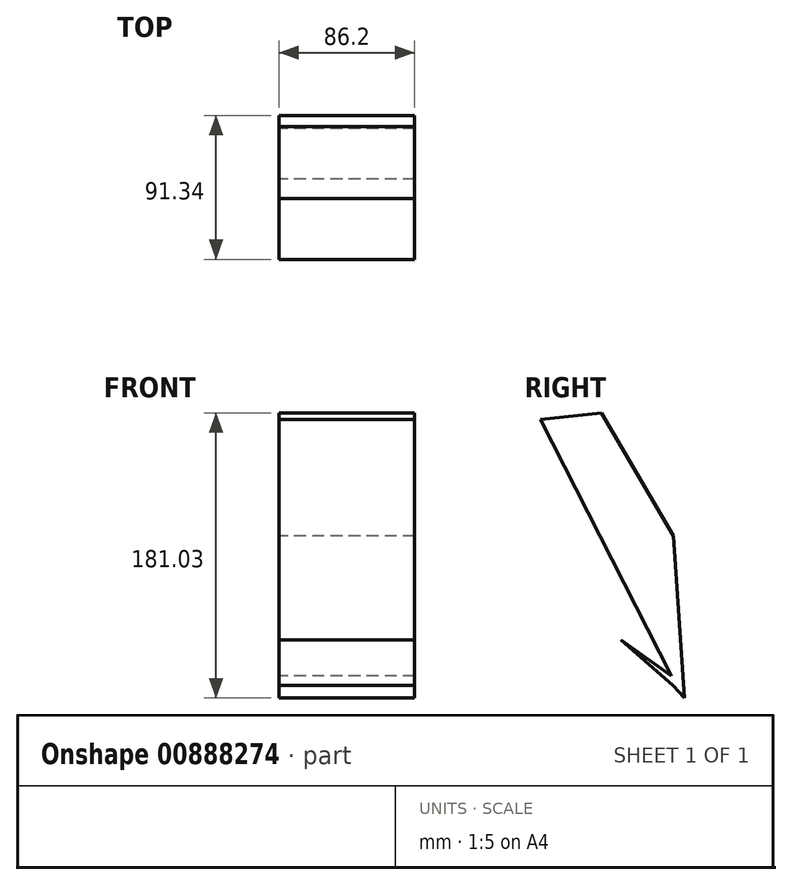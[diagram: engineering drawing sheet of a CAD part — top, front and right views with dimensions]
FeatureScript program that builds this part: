
annotation { "Feature Type Name" : "Feature", "Feature Type Description" : "" }
export const myFeature = defineFeature(function(context is Context, id is Id, definition is map)
    precondition{}
    {
        {
            var Q0;
            Q0=qCreatedBy(makeId("Right.planeOp"),FACE);
            var sketch = newSketch(context, id + "F0", { "sketchPlane" : qUnion([Q0])});
            skLineSegment(sketch, "E0", {"start": v(-30, -22.8) * mm, "end": v(-112.99, 140.07) * mm});
            skLineSegment(sketch, "E1", {"start": v(-112.99, 140.07) * mm, "end": v(-74.26, 144.22) * mm});
            skLineSegment(sketch, "E2", {"start": v(-74.26, 144.22) * mm, "end": v(-28.54, 66.04) * mm});
            skLineSegment(sketch, "E3", {"start": v(-28.54, 66.04) * mm, "end": v(-21.65, -36.8) * mm});
            skLineSegment(sketch, "E4", {"start": v(-21.65, -36.8) * mm, "end": v(-28.95, -29) * mm});
            skLineSegment(sketch, "E5", {"start": v(-28.95, -29) * mm, "end": v(-62.04, 0) * mm});
            skLineSegment(sketch, "E6", {"start": v(-62.04, 0) * mm, "end": v(-30, -22.8) * mm});
            skSolve(sketch);
        }
        {
            var Q0;
            Q0=makeQuery(id+"F0.imprint","IMPRINT",FACE,{"disambiguationData":[TD([[makeQuery(id+"F0.imprint","IMPRINT",EDGE,{"derivedFrom":sQuery(id+"F0.wireOp",EDGE,"E0")}),-1.0]])]});
            extrude(context, id + "F1", {"entities" : qUnion([Q0]), "depth" : 86.2 * mm, "offsetDistance" : 25.4 * mm});
        }
    });
